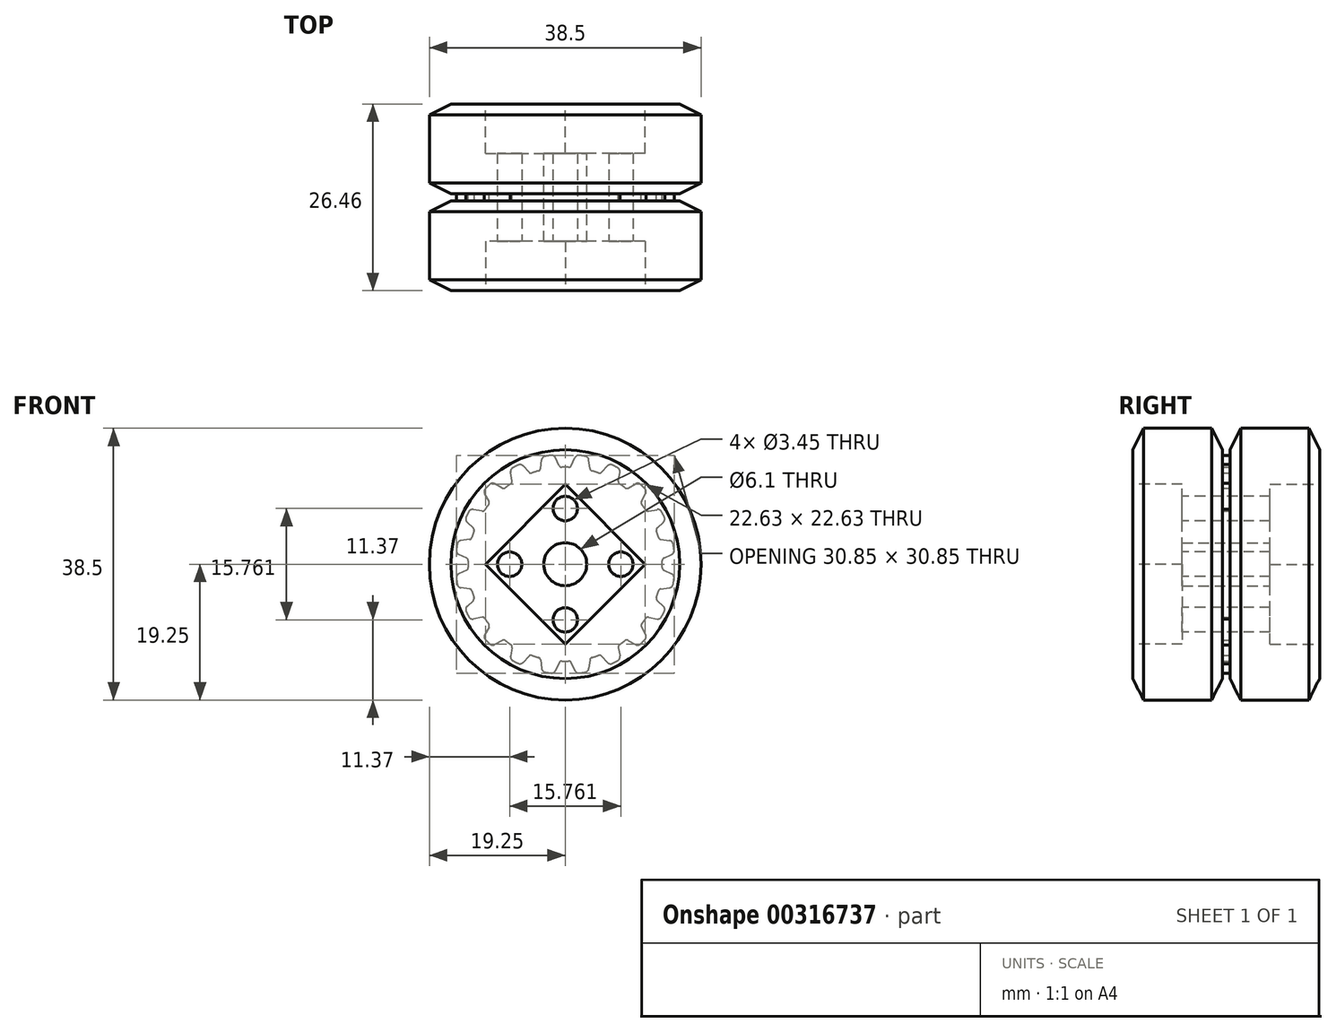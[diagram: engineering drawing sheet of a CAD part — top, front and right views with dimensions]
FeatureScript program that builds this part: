
annotation { "Feature Type Name" : "Feature", "Feature Type Description" : "" }
export const myFeature = defineFeature(function(context is Context, id is Id, definition is map)
    precondition{}
    {
        {
            var Q0;
            Q0=qCreatedBy(makeId("Front.planeOp"),FACE);
            var sketch = newSketch(context, id + "F0", { "sketchPlane" : qUnion([Q0])});
            skArc(sketch, "E0", {"start": v(-2, 15.42) * mm, "mid": v(-2.43, 15.36) * mm, "end": v(-2.86, 15.29) * mm});
            skArc(sketch, "E1", {"start": v(0.49, 13.74) * mm, "mid": v(0, 13.75) * mm, "end": v(-0.49, 13.74) * mm});
            skLineSegment(sketch, "E2", {"start": v(0, 0) * mm, "end": v(0, 13.75) * mm, "construction": true});
            skLineSegment(sketch, "E3", {"start": v(0.86, 13.97) * mm, "end": v(1.38, 15.08) * mm});
            skLineSegment(sketch, "E4", {"start": v(-0.86, 13.97) * mm, "end": v(-1.38, 15.08) * mm});
            skLineSegment(sketch, "E5", {"start": v(0, 13.75) * mm, "end": v(0, 15.55) * mm, "construction": true});
            skPoint(sketch, "E6.visualSharp", {"position": v(-1.56, 15.47) * mm});
            skArc(sketch, "E6.filletArc", {"start": v(-1.38, 15.08) * mm, "mid": v(-1.63, 15.35) * mm, "end": v(-2, 15.42) * mm});
            skPoint(sketch, "E7.visualSharp", {"position": v(1.56, 15.47) * mm});
            skArc(sketch, "E7.filletArc", {"start": v(2, 15.42) * mm, "mid": v(1.63, 15.35) * mm, "end": v(1.38, 15.08) * mm});
            skPoint(sketch, "E8.visualSharp", {"position": v(-0.75, 13.73) * mm});
            skArc(sketch, "E8.filletArc", {"start": v(-0.86, 13.97) * mm, "mid": v(-0.7, 13.8) * mm, "end": v(-0.49, 13.74) * mm});
            skPoint(sketch, "E9.visualSharp", {"position": v(0.75, 13.73) * mm});
            skArc(sketch, "E9.filletArc", {"start": v(0.49, 13.74) * mm, "mid": v(0.7, 13.8) * mm, "end": v(0.86, 13.97) * mm});
            skLineSegment(sketch, "E10.1.0", {"start": v(-4.25, 13.08) * mm, "end": v(-4.8, 14.8) * mm, "construction": true});
            skLineSegment(sketch, "E10.1.1", {"start": v(-5.14, 13.02) * mm, "end": v(-5.97, 13.92) * mm});
            skPoint(sketch, "E10.1.2", {"position": v(-6.27, 14.23) * mm});
            skPoint(sketch, "E10.1.3", {"position": v(-3.53, 13.3) * mm});
            skPoint(sketch, "E10.1.4", {"position": v(-4.96, 12.83) * mm});
            skPoint(sketch, "E10.1.5", {"position": v(-3.3, 15.2) * mm});
            skLineSegment(sketch, "E10.1.6", {"start": v(-3.5, 13.56) * mm, "end": v(-3.35, 14.77) * mm});
            skArc(sketch, "E10.1.7", {"start": v(-5.97, 13.92) * mm, "mid": v(-6.3, 14.1) * mm, "end": v(-6.67, 14.05) * mm});
            skArc(sketch, "E10.1.8", {"start": v(-2.86, 15.29) * mm, "mid": v(-3.2, 15.1) * mm, "end": v(-3.35, 14.77) * mm});
            skArc(sketch, "E10.1.9", {"start": v(-3.78, 13.22) * mm, "mid": v(-4.25, 13.08) * mm, "end": v(-4.7, 12.92) * mm});
            skArc(sketch, "E10.1.10", {"start": v(-3.78, 13.22) * mm, "mid": v(-3.6, 13.35) * mm, "end": v(-3.5, 13.56) * mm});
            skArc(sketch, "E10.1.11", {"start": v(-5.14, 13.02) * mm, "mid": v(-4.94, 12.9) * mm, "end": v(-4.7, 12.92) * mm});
            skLineSegment(sketch, "E10.2.0", {"start": v(-8.08, 11.13) * mm, "end": v(-9.14, 12.58) * mm, "construction": true});
            skLineSegment(sketch, "E10.2.1", {"start": v(-8.91, 10.8) * mm, "end": v(-9.98, 11.4) * mm});
            skPoint(sketch, "E10.2.2", {"position": v(-10.36, 11.6) * mm});
            skPoint(sketch, "E10.2.3", {"position": v(-7.46, 11.55) * mm});
            skPoint(sketch, "E10.2.4", {"position": v(-8.68, 10.67) * mm});
            skPoint(sketch, "E10.2.5", {"position": v(-7.83, 13.44) * mm});
            skLineSegment(sketch, "E10.2.6", {"start": v(-7.52, 11.81) * mm, "end": v(-7.75, 13.01) * mm});
            skArc(sketch, "E10.2.7", {"start": v(-9.98, 11.4) * mm, "mid": v(-10.35, 11.46) * mm, "end": v(-10.68, 11.3) * mm});
            skArc(sketch, "E10.2.8", {"start": v(-7.45, 13.65) * mm, "mid": v(-7.7, 13.38) * mm, "end": v(-7.75, 13.01) * mm});
            skArc(sketch, "E10.2.9", {"start": v(-7.68, 11.4) * mm, "mid": v(-8.08, 11.13) * mm, "end": v(-8.47, 10.83) * mm});
            skArc(sketch, "E10.2.10", {"start": v(-7.68, 11.4) * mm, "mid": v(-7.54, 11.58) * mm, "end": v(-7.52, 11.81) * mm});
            skArc(sketch, "E10.2.11", {"start": v(-8.91, 10.8) * mm, "mid": v(-8.69, 10.75) * mm, "end": v(-8.47, 10.83) * mm});
            skLineSegment(sketch, "E10.3.0", {"start": v(-11.13, 8.08) * mm, "end": v(-12.58, 9.14) * mm, "construction": true});
            skLineSegment(sketch, "E10.3.1", {"start": v(-11.81, 7.52) * mm, "end": v(-13.01, 7.75) * mm});
            skPoint(sketch, "E10.3.2", {"position": v(-13.44, 7.83) * mm});
            skPoint(sketch, "E10.3.3", {"position": v(-10.67, 8.68) * mm});
            skPoint(sketch, "E10.3.4", {"position": v(-11.55, 7.46) * mm});
            skPoint(sketch, "E10.3.5", {"position": v(-11.6, 10.36) * mm});
            skLineSegment(sketch, "E10.3.6", {"start": v(-10.8, 8.91) * mm, "end": v(-11.4, 9.98) * mm});
            skArc(sketch, "E10.3.7", {"start": v(-13.01, 7.75) * mm, "mid": v(-13.38, 7.7) * mm, "end": v(-13.65, 7.45) * mm});
            skArc(sketch, "E10.3.8", {"start": v(-11.3, 10.68) * mm, "mid": v(-11.46, 10.35) * mm, "end": v(-11.4, 9.98) * mm});
            skArc(sketch, "E10.3.9", {"start": v(-10.83, 8.47) * mm, "mid": v(-11.13, 8.08) * mm, "end": v(-11.4, 7.68) * mm});
            skArc(sketch, "E10.3.10", {"start": v(-10.83, 8.47) * mm, "mid": v(-10.75, 8.69) * mm, "end": v(-10.8, 8.91) * mm});
            skArc(sketch, "E10.3.11", {"start": v(-11.81, 7.52) * mm, "mid": v(-11.58, 7.54) * mm, "end": v(-11.4, 7.68) * mm});
            skLineSegment(sketch, "E10.4.0", {"start": v(-13.08, 4.25) * mm, "end": v(-14.8, 4.8) * mm, "construction": true});
            skLineSegment(sketch, "E10.4.1", {"start": v(-13.56, 3.5) * mm, "end": v(-14.77, 3.35) * mm});
            skPoint(sketch, "E10.4.2", {"position": v(-15.2, 3.3) * mm});
            skPoint(sketch, "E10.4.3", {"position": v(-12.83, 4.96) * mm});
            skPoint(sketch, "E10.4.4", {"position": v(-13.3, 3.53) * mm});
            skPoint(sketch, "E10.4.5", {"position": v(-14.23, 6.27) * mm});
            skLineSegment(sketch, "E10.4.6", {"start": v(-13.02, 5.14) * mm, "end": v(-13.92, 5.97) * mm});
            skArc(sketch, "E10.4.7", {"start": v(-14.77, 3.35) * mm, "mid": v(-15.1, 3.2) * mm, "end": v(-15.29, 2.86) * mm});
            skArc(sketch, "E10.4.8", {"start": v(-14.05, 6.67) * mm, "mid": v(-14.1, 6.3) * mm, "end": v(-13.92, 5.97) * mm});
            skArc(sketch, "E10.4.9", {"start": v(-12.92, 4.7) * mm, "mid": v(-13.08, 4.25) * mm, "end": v(-13.22, 3.78) * mm});
            skArc(sketch, "E10.4.10", {"start": v(-12.92, 4.7) * mm, "mid": v(-12.9, 4.94) * mm, "end": v(-13.02, 5.14) * mm});
            skArc(sketch, "E10.4.11", {"start": v(-13.56, 3.5) * mm, "mid": v(-13.35, 3.6) * mm, "end": v(-13.22, 3.78) * mm});
            skLineSegment(sketch, "E10.5.0", {"start": v(-13.75, 0) * mm, "end": v(-15.55, 0) * mm, "construction": true});
            skLineSegment(sketch, "E10.5.1", {"start": v(-13.97, -0.86) * mm, "end": v(-15.08, -1.38) * mm});
            skPoint(sketch, "E10.5.2", {"position": v(-15.47, -1.56) * mm});
            skPoint(sketch, "E10.5.3", {"position": v(-13.73, 0.75) * mm});
            skPoint(sketch, "E10.5.4", {"position": v(-13.73, -0.75) * mm});
            skPoint(sketch, "E10.5.5", {"position": v(-15.47, 1.56) * mm});
            skLineSegment(sketch, "E10.5.6", {"start": v(-13.97, 0.86) * mm, "end": v(-15.08, 1.38) * mm});
            skArc(sketch, "E10.5.7", {"start": v(-15.08, -1.38) * mm, "mid": v(-15.35, -1.63) * mm, "end": v(-15.42, -2) * mm});
            skArc(sketch, "E10.5.8", {"start": v(-15.42, 2) * mm, "mid": v(-15.35, 1.63) * mm, "end": v(-15.08, 1.38) * mm});
            skArc(sketch, "E10.5.9", {"start": v(-13.74, 0.49) * mm, "mid": v(-13.75, 0) * mm, "end": v(-13.74, -0.49) * mm});
            skArc(sketch, "E10.5.10", {"start": v(-13.74, 0.49) * mm, "mid": v(-13.8, 0.7) * mm, "end": v(-13.97, 0.86) * mm});
            skArc(sketch, "E10.5.11", {"start": v(-13.97, -0.86) * mm, "mid": v(-13.8, -0.7) * mm, "end": v(-13.74, -0.49) * mm});
            skLineSegment(sketch, "E10.6.0", {"start": v(-13.08, -4.25) * mm, "end": v(-14.8, -4.8) * mm, "construction": true});
            skLineSegment(sketch, "E10.6.1", {"start": v(-13.02, -5.14) * mm, "end": v(-13.92, -5.97) * mm});
            skPoint(sketch, "E10.6.2", {"position": v(-14.23, -6.27) * mm});
            skPoint(sketch, "E10.6.3", {"position": v(-13.3, -3.53) * mm});
            skPoint(sketch, "E10.6.4", {"position": v(-12.83, -4.96) * mm});
            skPoint(sketch, "E10.6.5", {"position": v(-15.2, -3.3) * mm});
            skLineSegment(sketch, "E10.6.6", {"start": v(-13.56, -3.5) * mm, "end": v(-14.77, -3.35) * mm});
            skArc(sketch, "E10.6.7", {"start": v(-13.92, -5.97) * mm, "mid": v(-14.1, -6.3) * mm, "end": v(-14.05, -6.67) * mm});
            skArc(sketch, "E10.6.8", {"start": v(-15.29, -2.86) * mm, "mid": v(-15.1, -3.2) * mm, "end": v(-14.77, -3.35) * mm});
            skArc(sketch, "E10.6.9", {"start": v(-13.22, -3.78) * mm, "mid": v(-13.08, -4.25) * mm, "end": v(-12.92, -4.7) * mm});
            skArc(sketch, "E10.6.10", {"start": v(-13.22, -3.78) * mm, "mid": v(-13.35, -3.6) * mm, "end": v(-13.56, -3.5) * mm});
            skArc(sketch, "E10.6.11", {"start": v(-13.02, -5.14) * mm, "mid": v(-12.9, -4.94) * mm, "end": v(-12.92, -4.7) * mm});
            skLineSegment(sketch, "E10.7.0", {"start": v(-11.13, -8.08) * mm, "end": v(-12.58, -9.14) * mm, "construction": true});
            skLineSegment(sketch, "E10.7.1", {"start": v(-10.8, -8.91) * mm, "end": v(-11.4, -9.98) * mm});
            skPoint(sketch, "E10.7.2", {"position": v(-11.6, -10.36) * mm});
            skPoint(sketch, "E10.7.3", {"position": v(-11.55, -7.46) * mm});
            skPoint(sketch, "E10.7.4", {"position": v(-10.67, -8.68) * mm});
            skPoint(sketch, "E10.7.5", {"position": v(-13.44, -7.83) * mm});
            skLineSegment(sketch, "E10.7.6", {"start": v(-11.81, -7.52) * mm, "end": v(-13.01, -7.75) * mm});
            skArc(sketch, "E10.7.7", {"start": v(-11.4, -9.98) * mm, "mid": v(-11.46, -10.35) * mm, "end": v(-11.3, -10.68) * mm});
            skArc(sketch, "E10.7.8", {"start": v(-13.65, -7.45) * mm, "mid": v(-13.38, -7.7) * mm, "end": v(-13.01, -7.75) * mm});
            skArc(sketch, "E10.7.9", {"start": v(-11.4, -7.68) * mm, "mid": v(-11.13, -8.08) * mm, "end": v(-10.83, -8.47) * mm});
            skArc(sketch, "E10.7.10", {"start": v(-11.4, -7.68) * mm, "mid": v(-11.58, -7.54) * mm, "end": v(-11.81, -7.52) * mm});
            skArc(sketch, "E10.7.11", {"start": v(-10.8, -8.91) * mm, "mid": v(-10.75, -8.69) * mm, "end": v(-10.83, -8.47) * mm});
            skLineSegment(sketch, "E10.8.0", {"start": v(-8.08, -11.13) * mm, "end": v(-9.14, -12.58) * mm, "construction": true});
            skLineSegment(sketch, "E10.8.1", {"start": v(-7.52, -11.81) * mm, "end": v(-7.75, -13.01) * mm});
            skPoint(sketch, "E10.8.2", {"position": v(-7.83, -13.44) * mm});
            skPoint(sketch, "E10.8.3", {"position": v(-8.68, -10.67) * mm});
            skPoint(sketch, "E10.8.4", {"position": v(-7.46, -11.55) * mm});
            skPoint(sketch, "E10.8.5", {"position": v(-10.36, -11.6) * mm});
            skLineSegment(sketch, "E10.8.6", {"start": v(-8.91, -10.8) * mm, "end": v(-9.98, -11.4) * mm});
            skArc(sketch, "E10.8.7", {"start": v(-7.75, -13.01) * mm, "mid": v(-7.7, -13.38) * mm, "end": v(-7.45, -13.65) * mm});
            skArc(sketch, "E10.8.8", {"start": v(-10.68, -11.3) * mm, "mid": v(-10.35, -11.46) * mm, "end": v(-9.98, -11.4) * mm});
            skArc(sketch, "E10.8.9", {"start": v(-8.47, -10.83) * mm, "mid": v(-8.08, -11.13) * mm, "end": v(-7.68, -11.4) * mm});
            skArc(sketch, "E10.8.10", {"start": v(-8.47, -10.83) * mm, "mid": v(-8.69, -10.75) * mm, "end": v(-8.91, -10.8) * mm});
            skArc(sketch, "E10.8.11", {"start": v(-7.52, -11.81) * mm, "mid": v(-7.54, -11.58) * mm, "end": v(-7.68, -11.4) * mm});
            skLineSegment(sketch, "E10.9.0", {"start": v(-4.25, -13.08) * mm, "end": v(-4.8, -14.8) * mm, "construction": true});
            skLineSegment(sketch, "E10.9.1", {"start": v(-3.5, -13.56) * mm, "end": v(-3.35, -14.77) * mm});
            skPoint(sketch, "E10.9.2", {"position": v(-3.3, -15.2) * mm});
            skPoint(sketch, "E10.9.3", {"position": v(-4.96, -12.83) * mm});
            skPoint(sketch, "E10.9.4", {"position": v(-3.53, -13.3) * mm});
            skPoint(sketch, "E10.9.5", {"position": v(-6.27, -14.23) * mm});
            skLineSegment(sketch, "E10.9.6", {"start": v(-5.14, -13.02) * mm, "end": v(-5.97, -13.92) * mm});
            skArc(sketch, "E10.9.7", {"start": v(-3.35, -14.77) * mm, "mid": v(-3.2, -15.1) * mm, "end": v(-2.86, -15.29) * mm});
            skArc(sketch, "E10.9.8", {"start": v(-6.67, -14.05) * mm, "mid": v(-6.3, -14.1) * mm, "end": v(-5.97, -13.92) * mm});
            skArc(sketch, "E10.9.9", {"start": v(-4.7, -12.92) * mm, "mid": v(-4.25, -13.08) * mm, "end": v(-3.78, -13.22) * mm});
            skArc(sketch, "E10.9.10", {"start": v(-4.7, -12.92) * mm, "mid": v(-4.94, -12.9) * mm, "end": v(-5.14, -13.02) * mm});
            skArc(sketch, "E10.9.11", {"start": v(-3.5, -13.56) * mm, "mid": v(-3.6, -13.35) * mm, "end": v(-3.78, -13.22) * mm});
            skLineSegment(sketch, "E10.10.0", {"start": v(0, -13.75) * mm, "end": v(0, -15.55) * mm, "construction": true});
            skLineSegment(sketch, "E10.10.1", {"start": v(0.86, -13.97) * mm, "end": v(1.38, -15.08) * mm});
            skPoint(sketch, "E10.10.2", {"position": v(1.56, -15.47) * mm});
            skPoint(sketch, "E10.10.3", {"position": v(-0.75, -13.73) * mm});
            skPoint(sketch, "E10.10.4", {"position": v(0.75, -13.73) * mm});
            skPoint(sketch, "E10.10.5", {"position": v(-1.56, -15.47) * mm});
            skLineSegment(sketch, "E10.10.6", {"start": v(-0.86, -13.97) * mm, "end": v(-1.38, -15.08) * mm});
            skArc(sketch, "E10.10.7", {"start": v(1.38, -15.08) * mm, "mid": v(1.63, -15.35) * mm, "end": v(2, -15.42) * mm});
            skArc(sketch, "E10.10.8", {"start": v(-2, -15.42) * mm, "mid": v(-1.63, -15.35) * mm, "end": v(-1.38, -15.08) * mm});
            skArc(sketch, "E10.10.9", {"start": v(-0.49, -13.74) * mm, "mid": v(0, -13.75) * mm, "end": v(0.49, -13.74) * mm});
            skArc(sketch, "E10.10.10", {"start": v(-0.49, -13.74) * mm, "mid": v(-0.7, -13.8) * mm, "end": v(-0.86, -13.97) * mm});
            skArc(sketch, "E10.10.11", {"start": v(0.86, -13.97) * mm, "mid": v(0.7, -13.8) * mm, "end": v(0.49, -13.74) * mm});
            skLineSegment(sketch, "E10.11.0", {"start": v(4.25, -13.08) * mm, "end": v(4.8, -14.8) * mm, "construction": true});
            skLineSegment(sketch, "E10.11.1", {"start": v(5.14, -13.02) * mm, "end": v(5.97, -13.92) * mm});
            skPoint(sketch, "E10.11.2", {"position": v(6.27, -14.23) * mm});
            skPoint(sketch, "E10.11.3", {"position": v(3.53, -13.3) * mm});
            skPoint(sketch, "E10.11.4", {"position": v(4.96, -12.83) * mm});
            skPoint(sketch, "E10.11.5", {"position": v(3.3, -15.2) * mm});
            skLineSegment(sketch, "E10.11.6", {"start": v(3.5, -13.56) * mm, "end": v(3.35, -14.77) * mm});
            skArc(sketch, "E10.11.7", {"start": v(5.97, -13.92) * mm, "mid": v(6.3, -14.1) * mm, "end": v(6.67, -14.05) * mm});
            skArc(sketch, "E10.11.8", {"start": v(2.86, -15.29) * mm, "mid": v(3.2, -15.1) * mm, "end": v(3.35, -14.77) * mm});
            skArc(sketch, "E10.11.9", {"start": v(3.78, -13.22) * mm, "mid": v(4.25, -13.08) * mm, "end": v(4.7, -12.92) * mm});
            skArc(sketch, "E10.11.10", {"start": v(3.78, -13.22) * mm, "mid": v(3.6, -13.35) * mm, "end": v(3.5, -13.56) * mm});
            skArc(sketch, "E10.11.11", {"start": v(5.14, -13.02) * mm, "mid": v(4.94, -12.9) * mm, "end": v(4.7, -12.92) * mm});
            skLineSegment(sketch, "E10.12.0", {"start": v(8.08, -11.13) * mm, "end": v(9.14, -12.58) * mm, "construction": true});
            skLineSegment(sketch, "E10.12.1", {"start": v(8.91, -10.8) * mm, "end": v(9.98, -11.4) * mm});
            skPoint(sketch, "E10.12.2", {"position": v(10.36, -11.6) * mm});
            skPoint(sketch, "E10.12.3", {"position": v(7.46, -11.55) * mm});
            skPoint(sketch, "E10.12.4", {"position": v(8.68, -10.67) * mm});
            skPoint(sketch, "E10.12.5", {"position": v(7.83, -13.44) * mm});
            skLineSegment(sketch, "E10.12.6", {"start": v(7.52, -11.81) * mm, "end": v(7.75, -13.01) * mm});
            skArc(sketch, "E10.12.7", {"start": v(9.98, -11.4) * mm, "mid": v(10.35, -11.46) * mm, "end": v(10.68, -11.3) * mm});
            skArc(sketch, "E10.12.8", {"start": v(7.45, -13.65) * mm, "mid": v(7.7, -13.38) * mm, "end": v(7.75, -13.01) * mm});
            skArc(sketch, "E10.12.9", {"start": v(7.68, -11.4) * mm, "mid": v(8.08, -11.13) * mm, "end": v(8.47, -10.83) * mm});
            skArc(sketch, "E10.12.10", {"start": v(7.68, -11.4) * mm, "mid": v(7.54, -11.58) * mm, "end": v(7.52, -11.81) * mm});
            skArc(sketch, "E10.12.11", {"start": v(8.91, -10.8) * mm, "mid": v(8.69, -10.75) * mm, "end": v(8.47, -10.83) * mm});
            skLineSegment(sketch, "E10.13.0", {"start": v(11.13, -8.08) * mm, "end": v(12.58, -9.14) * mm, "construction": true});
            skLineSegment(sketch, "E10.13.1", {"start": v(11.81, -7.52) * mm, "end": v(13.01, -7.75) * mm});
            skPoint(sketch, "E10.13.2", {"position": v(13.44, -7.83) * mm});
            skPoint(sketch, "E10.13.3", {"position": v(10.67, -8.68) * mm});
            skPoint(sketch, "E10.13.4", {"position": v(11.55, -7.46) * mm});
            skPoint(sketch, "E10.13.5", {"position": v(11.6, -10.36) * mm});
            skLineSegment(sketch, "E10.13.6", {"start": v(10.8, -8.91) * mm, "end": v(11.4, -9.98) * mm});
            skArc(sketch, "E10.13.7", {"start": v(13.01, -7.75) * mm, "mid": v(13.38, -7.7) * mm, "end": v(13.65, -7.45) * mm});
            skArc(sketch, "E10.13.8", {"start": v(11.3, -10.68) * mm, "mid": v(11.46, -10.35) * mm, "end": v(11.4, -9.98) * mm});
            skArc(sketch, "E10.13.9", {"start": v(10.83, -8.47) * mm, "mid": v(11.13, -8.08) * mm, "end": v(11.4, -7.68) * mm});
            skArc(sketch, "E10.13.10", {"start": v(10.83, -8.47) * mm, "mid": v(10.75, -8.69) * mm, "end": v(10.8, -8.91) * mm});
            skArc(sketch, "E10.13.11", {"start": v(11.81, -7.52) * mm, "mid": v(11.58, -7.54) * mm, "end": v(11.4, -7.68) * mm});
            skLineSegment(sketch, "E10.14.0", {"start": v(13.08, -4.25) * mm, "end": v(14.8, -4.8) * mm, "construction": true});
            skLineSegment(sketch, "E10.14.1", {"start": v(13.56, -3.5) * mm, "end": v(14.77, -3.35) * mm});
            skPoint(sketch, "E10.14.2", {"position": v(15.2, -3.3) * mm});
            skPoint(sketch, "E10.14.3", {"position": v(12.83, -4.96) * mm});
            skPoint(sketch, "E10.14.4", {"position": v(13.3, -3.53) * mm});
            skPoint(sketch, "E10.14.5", {"position": v(14.23, -6.27) * mm});
            skLineSegment(sketch, "E10.14.6", {"start": v(13.02, -5.14) * mm, "end": v(13.92, -5.97) * mm});
            skArc(sketch, "E10.14.7", {"start": v(14.77, -3.35) * mm, "mid": v(15.1, -3.2) * mm, "end": v(15.29, -2.86) * mm});
            skArc(sketch, "E10.14.8", {"start": v(14.05, -6.67) * mm, "mid": v(14.1, -6.3) * mm, "end": v(13.92, -5.97) * mm});
            skArc(sketch, "E10.14.9", {"start": v(12.92, -4.7) * mm, "mid": v(13.08, -4.25) * mm, "end": v(13.22, -3.78) * mm});
            skArc(sketch, "E10.14.10", {"start": v(12.92, -4.7) * mm, "mid": v(12.9, -4.94) * mm, "end": v(13.02, -5.14) * mm});
            skArc(sketch, "E10.14.11", {"start": v(13.56, -3.5) * mm, "mid": v(13.35, -3.6) * mm, "end": v(13.22, -3.78) * mm});
            skLineSegment(sketch, "E10.15.0", {"start": v(13.75, 0) * mm, "end": v(15.55, 0) * mm, "construction": true});
            skLineSegment(sketch, "E10.15.1", {"start": v(13.97, 0.86) * mm, "end": v(15.08, 1.38) * mm});
            skPoint(sketch, "E10.15.2", {"position": v(15.47, 1.56) * mm});
            skPoint(sketch, "E10.15.3", {"position": v(13.73, -0.75) * mm});
            skPoint(sketch, "E10.15.4", {"position": v(13.73, 0.75) * mm});
            skPoint(sketch, "E10.15.5", {"position": v(15.47, -1.56) * mm});
            skLineSegment(sketch, "E10.15.6", {"start": v(13.97, -0.86) * mm, "end": v(15.08, -1.38) * mm});
            skArc(sketch, "E10.15.7", {"start": v(15.08, 1.38) * mm, "mid": v(15.35, 1.63) * mm, "end": v(15.42, 2) * mm});
            skArc(sketch, "E10.15.8", {"start": v(15.42, -2) * mm, "mid": v(15.35, -1.63) * mm, "end": v(15.08, -1.38) * mm});
            skArc(sketch, "E10.15.9", {"start": v(13.74, -0.49) * mm, "mid": v(13.75, 0) * mm, "end": v(13.74, 0.49) * mm});
            skArc(sketch, "E10.15.10", {"start": v(13.74, -0.49) * mm, "mid": v(13.8, -0.7) * mm, "end": v(13.97, -0.86) * mm});
            skArc(sketch, "E10.15.11", {"start": v(13.97, 0.86) * mm, "mid": v(13.8, 0.7) * mm, "end": v(13.74, 0.49) * mm});
            skArc(sketch, "E11.trimOffspring", {"start": v(2.86, 15.29) * mm, "mid": v(2.43, 15.36) * mm, "end": v(2, 15.42) * mm});
            skArc(sketch, "E12.trimOffspring", {"start": v(15.29, -2.86) * mm, "mid": v(15.36, -2.43) * mm, "end": v(15.42, -2) * mm});
            skArc(sketch, "E13.trimOffspring", {"start": v(13.65, -7.45) * mm, "mid": v(13.86, -7.06) * mm, "end": v(14.05, -6.67) * mm});
            skArc(sketch, "E14.trimOffspring", {"start": v(10.68, -11.3) * mm, "mid": v(11, -11) * mm, "end": v(11.3, -10.68) * mm});
            skArc(sketch, "E15.trimOffspring", {"start": v(6.67, -14.05) * mm, "mid": v(7.06, -13.86) * mm, "end": v(7.45, -13.65) * mm});
            skArc(sketch, "E16.trimOffspring", {"start": v(2, -15.42) * mm, "mid": v(2.43, -15.36) * mm, "end": v(2.86, -15.29) * mm});
            skArc(sketch, "E17.trimOffspring", {"start": v(-2.86, -15.29) * mm, "mid": v(-2.43, -15.36) * mm, "end": v(-2, -15.42) * mm});
            skArc(sketch, "E18.trimOffspring", {"start": v(-7.45, -13.65) * mm, "mid": v(-7.06, -13.86) * mm, "end": v(-6.67, -14.05) * mm});
            skArc(sketch, "E19.trimOffspring", {"start": v(-11.3, -10.68) * mm, "mid": v(-11, -11) * mm, "end": v(-10.68, -11.3) * mm});
            skArc(sketch, "E20.trimOffspring", {"start": v(-14.05, -6.67) * mm, "mid": v(-13.86, -7.06) * mm, "end": v(-13.65, -7.45) * mm});
            skArc(sketch, "E21.trimOffspring", {"start": v(-15.42, -2) * mm, "mid": v(-15.36, -2.43) * mm, "end": v(-15.29, -2.86) * mm});
            skArc(sketch, "E22.trimOffspring", {"start": v(-15.29, 2.86) * mm, "mid": v(-15.36, 2.43) * mm, "end": v(-15.42, 2) * mm});
            skArc(sketch, "E23.trimOffspring", {"start": v(-13.65, 7.45) * mm, "mid": v(-13.86, 7.06) * mm, "end": v(-14.05, 6.67) * mm});
            skArc(sketch, "E24.trimOffspring", {"start": v(-10.68, 11.3) * mm, "mid": v(-11, 11) * mm, "end": v(-11.3, 10.68) * mm});
            skArc(sketch, "E25.trimOffspring", {"start": v(-6.67, 14.05) * mm, "mid": v(-7.06, 13.86) * mm, "end": v(-7.45, 13.65) * mm});
            skArc(sketch, "E26", {"start": v(14.05, 6.67) * mm, "mid": v(13.86, 7.06) * mm, "end": v(13.65, 7.45) * mm, "construction": true});
            skCircle(sketch, "E27", {"center": v(0, 0) * mm, "radius": 13.75 * mm, "construction": true});
            skCircle(sketch, "E28", {"center": v(0, 0) * mm, "radius": 15.98 * mm, "construction": true});
            skLineSegment(sketch, "E29", {"start": v(0, 15.55) * mm, "end": v(0, 15.98) * mm, "construction": true});
            skLineSegment(sketch, "E30", {"start": v(4.8, 14.8) * mm, "end": v(4.94, 15.2) * mm, "construction": true});
            skLineSegment(sketch, "E31.3.16.0", {"start": v(13.02, 5.14) * mm, "end": v(13.92, 5.97) * mm});
            skPoint(sketch, "E31.6.16.0", {"position": v(14.23, 6.27) * mm});
            skPoint(sketch, "E31.7.16.0", {"position": v(13.3, 3.53) * mm});
            skPoint(sketch, "E31.8.16.0", {"position": v(12.83, 4.96) * mm});
            skPoint(sketch, "E31.9.16.0", {"position": v(15.2, 3.3) * mm});
            skLineSegment(sketch, "E31.10.16.0", {"start": v(13.56, 3.5) * mm, "end": v(14.77, 3.35) * mm});
            skArc(sketch, "E31.13.16.0", {"start": v(13.92, 5.97) * mm, "mid": v(14.1, 6.3) * mm, "end": v(14.05, 6.67) * mm});
            skLineSegment(sketch, "E31.14.16.0", {"start": v(13.08, 4.25) * mm, "end": v(14.8, 4.8) * mm, "construction": true});
            skArc(sketch, "E31.17.16.0", {"start": v(15.29, 2.86) * mm, "mid": v(15.1, 3.2) * mm, "end": v(14.77, 3.35) * mm});
            skArc(sketch, "E31.21.16.0", {"start": v(13.22, 3.78) * mm, "mid": v(13.08, 4.25) * mm, "end": v(12.92, 4.7) * mm});
            skArc(sketch, "E31.25.16.0", {"start": v(13.22, 3.78) * mm, "mid": v(13.35, 3.6) * mm, "end": v(13.56, 3.5) * mm});
            skArc(sketch, "E31.29.16.0", {"start": v(13.02, 5.14) * mm, "mid": v(12.9, 4.94) * mm, "end": v(12.92, 4.7) * mm});
            skLineSegment(sketch, "E31.3.17.0", {"start": v(10.8, 8.91) * mm, "end": v(11.4, 9.98) * mm});
            skPoint(sketch, "E31.6.17.0", {"position": v(11.6, 10.36) * mm});
            skPoint(sketch, "E31.7.17.0", {"position": v(11.55, 7.46) * mm});
            skPoint(sketch, "E31.8.17.0", {"position": v(10.67, 8.68) * mm});
            skPoint(sketch, "E31.9.17.0", {"position": v(13.44, 7.83) * mm});
            skLineSegment(sketch, "E31.10.17.0", {"start": v(11.81, 7.52) * mm, "end": v(13.01, 7.75) * mm});
            skArc(sketch, "E31.13.17.0", {"start": v(11.4, 9.98) * mm, "mid": v(11.46, 10.35) * mm, "end": v(11.3, 10.68) * mm});
            skLineSegment(sketch, "E31.14.17.0", {"start": v(11.13, 8.08) * mm, "end": v(12.58, 9.14) * mm, "construction": true});
            skArc(sketch, "E31.17.17.0", {"start": v(13.65, 7.45) * mm, "mid": v(13.38, 7.7) * mm, "end": v(13.01, 7.75) * mm});
            skArc(sketch, "E31.21.17.0", {"start": v(11.4, 7.68) * mm, "mid": v(11.13, 8.08) * mm, "end": v(10.83, 8.47) * mm});
            skArc(sketch, "E31.25.17.0", {"start": v(11.4, 7.68) * mm, "mid": v(11.58, 7.54) * mm, "end": v(11.81, 7.52) * mm});
            skArc(sketch, "E31.29.17.0", {"start": v(10.8, 8.91) * mm, "mid": v(10.75, 8.69) * mm, "end": v(10.83, 8.47) * mm});
            skLineSegment(sketch, "E31.3.18.0", {"start": v(7.52, 11.81) * mm, "end": v(7.75, 13.01) * mm});
            skPoint(sketch, "E31.7.18.0", {"position": v(8.68, 10.67) * mm});
            skPoint(sketch, "E31.8.18.0", {"position": v(7.46, 11.55) * mm});
            skPoint(sketch, "E31.9.18.0", {"position": v(10.36, 11.6) * mm});
            skLineSegment(sketch, "E31.10.18.0", {"start": v(8.91, 10.8) * mm, "end": v(9.98, 11.4) * mm});
            skArc(sketch, "E31.13.18.0", {"start": v(7.75, 13.01) * mm, "mid": v(7.7, 13.38) * mm, "end": v(7.45, 13.65) * mm});
            skLineSegment(sketch, "E31.14.18.0", {"start": v(8.08, 11.13) * mm, "end": v(9.14, 12.58) * mm, "construction": true});
            skArc(sketch, "E31.17.18.0", {"start": v(10.68, 11.3) * mm, "mid": v(10.35, 11.46) * mm, "end": v(9.98, 11.4) * mm});
            skArc(sketch, "E31.21.18.0", {"start": v(8.47, 10.83) * mm, "mid": v(8.08, 11.13) * mm, "end": v(7.68, 11.4) * mm});
            skArc(sketch, "E31.25.18.0", {"start": v(8.47, 10.83) * mm, "mid": v(8.69, 10.75) * mm, "end": v(8.91, 10.8) * mm});
            skArc(sketch, "E31.29.18.0", {"start": v(7.52, 11.81) * mm, "mid": v(7.54, 11.58) * mm, "end": v(7.68, 11.4) * mm});
            skLineSegment(sketch, "E31.3.19.0", {"start": v(3.5, 13.56) * mm, "end": v(3.35, 14.77) * mm});
            skPoint(sketch, "E31.6.19.0", {"position": v(3.3, 15.2) * mm});
            skPoint(sketch, "E31.7.19.0", {"position": v(4.96, 12.83) * mm});
            skPoint(sketch, "E31.8.19.0", {"position": v(3.53, 13.3) * mm});
            skPoint(sketch, "E31.9.19.0", {"position": v(6.27, 14.23) * mm});
            skLineSegment(sketch, "E31.10.19.0", {"start": v(5.14, 13.02) * mm, "end": v(5.97, 13.92) * mm});
            skArc(sketch, "E31.13.19.0", {"start": v(3.35, 14.77) * mm, "mid": v(3.2, 15.1) * mm, "end": v(2.86, 15.29) * mm});
            skLineSegment(sketch, "E31.14.19.0", {"start": v(4.25, 13.08) * mm, "end": v(4.8, 14.8) * mm, "construction": true});
            skArc(sketch, "E31.17.19.0", {"start": v(6.67, 14.05) * mm, "mid": v(6.3, 14.1) * mm, "end": v(5.97, 13.92) * mm});
            skArc(sketch, "E31.21.19.0", {"start": v(4.7, 12.92) * mm, "mid": v(4.25, 13.08) * mm, "end": v(3.78, 13.22) * mm});
            skArc(sketch, "E31.25.19.0", {"start": v(4.7, 12.92) * mm, "mid": v(4.94, 12.9) * mm, "end": v(5.14, 13.02) * mm});
            skArc(sketch, "E31.29.19.0", {"start": v(3.5, 13.56) * mm, "mid": v(3.6, 13.35) * mm, "end": v(3.78, 13.22) * mm});
            skArc(sketch, "E32.trimOffspring", {"start": v(14.05, 6.67) * mm, "mid": v(13.86, 7.06) * mm, "end": v(13.65, 7.45) * mm});
            skArc(sketch, "E33.trimOffspring", {"start": v(7.45, 13.65) * mm, "mid": v(-13.86, -7.06) * mm, "end": v(15.42, -2) * mm, "construction": true});
            skArc(sketch, "E34.trimOffspring", {"start": v(7.45, 13.65) * mm, "mid": v(7.06, 13.86) * mm, "end": v(6.67, 14.05) * mm});
            skArc(sketch, "E35.trimOffspring", {"start": v(11.3, 10.68) * mm, "mid": v(11, 11) * mm, "end": v(10.68, 11.3) * mm, "construction": true});
            skArc(sketch, "E36.trimOffspring", {"start": v(11.3, 10.68) * mm, "mid": v(11, 11) * mm, "end": v(10.68, 11.3) * mm});
            skArc(sketch, "E37.trimOffspring", {"start": v(15.42, 2) * mm, "mid": v(15.36, 2.43) * mm, "end": v(15.29, 2.86) * mm, "construction": true});
            skArc(sketch, "E38.trimOffspring", {"start": v(15.42, 2) * mm, "mid": v(15.36, 2.43) * mm, "end": v(15.29, 2.86) * mm});
            skSolve(sketch);
        }
        {
            var Q0;
            Q0 = qSketchRegion(id + "F0", true);
            extrude(context, id + "F1", {"entities" : qUnion([Q0]), "depth" : ((27 / 25.4) / 2) * mm});
        }
        {
            var Q0;
            Q0=makeQuery(id+"F1.opExtrude","CAP_FACE",FACE,{"disambiguationData":[OSD([sQuery(id+"F0.wireOp",EDGE,"E0"),sQuery(id+"F0.wireOp",EDGE,"E1"),sQuery(id+"F0.wireOp",EDGE,"E3"),sQuery(id+"F0.wireOp",EDGE,"E4"),sQuery(id+"F0.wireOp",EDGE,"E6.filletArc"),sQuery(id+"F0.wireOp",EDGE,"E7.filletArc"),sQuery(id+"F0.wireOp",EDGE,"E8.filletArc"),sQuery(id+"F0.wireOp",EDGE,"E9.filletArc"),sQuery(id+"F0.wireOp",EDGE,"E10.1.1"),sQuery(id+"F0.wireOp",EDGE,"E10.1.6"),sQuery(id+"F0.wireOp",EDGE,"E10.1.7"),sQuery(id+"F0.wireOp",EDGE,"E10.1.8"),sQuery(id+"F0.wireOp",EDGE,"E10.1.9"),sQuery(id+"F0.wireOp",EDGE,"E10.1.10"),sQuery(id+"F0.wireOp",EDGE,"E10.1.11"),sQuery(id+"F0.wireOp",EDGE,"E10.2.1"),sQuery(id+"F0.wireOp",EDGE,"E10.2.6"),sQuery(id+"F0.wireOp",EDGE,"E10.2.7"),sQuery(id+"F0.wireOp",EDGE,"E10.2.8"),sQuery(id+"F0.wireOp",EDGE,"E10.2.9"),sQuery(id+"F0.wireOp",EDGE,"E10.2.10"),sQuery(id+"F0.wireOp",EDGE,"E10.2.11"),sQuery(id+"F0.wireOp",EDGE,"E10.3.1"),sQuery(id+"F0.wireOp",EDGE,"E10.3.6"),sQuery(id+"F0.wireOp",EDGE,"E10.3.7"),sQuery(id+"F0.wireOp",EDGE,"E10.3.8"),sQuery(id+"F0.wireOp",EDGE,"E10.3.9"),sQuery(id+"F0.wireOp",EDGE,"E10.3.10"),sQuery(id+"F0.wireOp",EDGE,"E10.3.11"),sQuery(id+"F0.wireOp",EDGE,"E10.4.1"),sQuery(id+"F0.wireOp",EDGE,"E10.4.6"),sQuery(id+"F0.wireOp",EDGE,"E10.4.7"),sQuery(id+"F0.wireOp",EDGE,"E10.4.8"),sQuery(id+"F0.wireOp",EDGE,"E10.4.9"),sQuery(id+"F0.wireOp",EDGE,"E10.4.10"),sQuery(id+"F0.wireOp",EDGE,"E10.4.11"),sQuery(id+"F0.wireOp",EDGE,"E10.5.1"),sQuery(id+"F0.wireOp",EDGE,"E10.5.6"),sQuery(id+"F0.wireOp",EDGE,"E10.5.7"),sQuery(id+"F0.wireOp",EDGE,"E10.5.8"),sQuery(id+"F0.wireOp",EDGE,"E10.5.9"),sQuery(id+"F0.wireOp",EDGE,"E10.5.10"),sQuery(id+"F0.wireOp",EDGE,"E10.5.11"),sQuery(id+"F0.wireOp",EDGE,"E10.6.1"),sQuery(id+"F0.wireOp",EDGE,"E10.6.6"),sQuery(id+"F0.wireOp",EDGE,"E10.6.7"),sQuery(id+"F0.wireOp",EDGE,"E10.6.8"),sQuery(id+"F0.wireOp",EDGE,"E10.6.9"),sQuery(id+"F0.wireOp",EDGE,"E10.6.10"),sQuery(id+"F0.wireOp",EDGE,"E10.6.11"),sQuery(id+"F0.wireOp",EDGE,"E10.7.1"),sQuery(id+"F0.wireOp",EDGE,"E10.7.6"),sQuery(id+"F0.wireOp",EDGE,"E10.7.7"),sQuery(id+"F0.wireOp",EDGE,"E10.7.8"),sQuery(id+"F0.wireOp",EDGE,"E10.7.9"),sQuery(id+"F0.wireOp",EDGE,"E10.7.10"),sQuery(id+"F0.wireOp",EDGE,"E10.7.11"),sQuery(id+"F0.wireOp",EDGE,"E10.8.1"),sQuery(id+"F0.wireOp",EDGE,"E10.8.6"),sQuery(id+"F0.wireOp",EDGE,"E10.8.7"),sQuery(id+"F0.wireOp",EDGE,"E10.8.8"),sQuery(id+"F0.wireOp",EDGE,"E10.8.9"),sQuery(id+"F0.wireOp",EDGE,"E10.8.10"),sQuery(id+"F0.wireOp",EDGE,"E10.8.11"),sQuery(id+"F0.wireOp",EDGE,"E10.9.1"),sQuery(id+"F0.wireOp",EDGE,"E10.9.6"),sQuery(id+"F0.wireOp",EDGE,"E10.9.7"),sQuery(id+"F0.wireOp",EDGE,"E10.9.8"),sQuery(id+"F0.wireOp",EDGE,"E10.9.9"),sQuery(id+"F0.wireOp",EDGE,"E10.9.10"),sQuery(id+"F0.wireOp",EDGE,"E10.9.11"),sQuery(id+"F0.wireOp",EDGE,"E10.10.1"),sQuery(id+"F0.wireOp",EDGE,"E10.10.6"),sQuery(id+"F0.wireOp",EDGE,"E10.10.7"),sQuery(id+"F0.wireOp",EDGE,"E10.10.8"),sQuery(id+"F0.wireOp",EDGE,"E10.10.9"),sQuery(id+"F0.wireOp",EDGE,"E10.10.10"),sQuery(id+"F0.wireOp",EDGE,"E10.10.11"),sQuery(id+"F0.wireOp",EDGE,"E10.11.1"),sQuery(id+"F0.wireOp",EDGE,"E10.11.6"),sQuery(id+"F0.wireOp",EDGE,"E10.11.7"),sQuery(id+"F0.wireOp",EDGE,"E10.11.8"),sQuery(id+"F0.wireOp",EDGE,"E10.11.9"),sQuery(id+"F0.wireOp",EDGE,"E10.11.10"),sQuery(id+"F0.wireOp",EDGE,"E10.11.11"),sQuery(id+"F0.wireOp",EDGE,"E10.12.1"),sQuery(id+"F0.wireOp",EDGE,"E10.12.6"),sQuery(id+"F0.wireOp",EDGE,"E10.12.7"),sQuery(id+"F0.wireOp",EDGE,"E10.12.8"),sQuery(id+"F0.wireOp",EDGE,"E10.12.9"),sQuery(id+"F0.wireOp",EDGE,"E10.12.10"),sQuery(id+"F0.wireOp",EDGE,"E10.12.11"),sQuery(id+"F0.wireOp",EDGE,"E10.13.1"),sQuery(id+"F0.wireOp",EDGE,"E10.13.6"),sQuery(id+"F0.wireOp",EDGE,"E10.13.7"),sQuery(id+"F0.wireOp",EDGE,"E10.13.8"),sQuery(id+"F0.wireOp",EDGE,"E10.13.9"),sQuery(id+"F0.wireOp",EDGE,"E10.13.10"),sQuery(id+"F0.wireOp",EDGE,"E10.13.11"),sQuery(id+"F0.wireOp",EDGE,"E10.14.1"),sQuery(id+"F0.wireOp",EDGE,"E10.14.6"),sQuery(id+"F0.wireOp",EDGE,"E10.14.7"),sQuery(id+"F0.wireOp",EDGE,"E10.14.8"),sQuery(id+"F0.wireOp",EDGE,"E10.14.9"),sQuery(id+"F0.wireOp",EDGE,"E10.14.10"),sQuery(id+"F0.wireOp",EDGE,"E10.14.11"),sQuery(id+"F0.wireOp",EDGE,"E10.15.1"),sQuery(id+"F0.wireOp",EDGE,"E10.15.6"),sQuery(id+"F0.wireOp",EDGE,"E10.15.7"),sQuery(id+"F0.wireOp",EDGE,"E10.15.8"),sQuery(id+"F0.wireOp",EDGE,"E10.15.9"),sQuery(id+"F0.wireOp",EDGE,"E10.15.10"),sQuery(id+"F0.wireOp",EDGE,"E10.15.11"),sQuery(id+"F0.wireOp",EDGE,"E11.trimOffspring"),sQuery(id+"F0.wireOp",EDGE,"E12.trimOffspring"),sQuery(id+"F0.wireOp",EDGE,"E13.trimOffspring"),sQuery(id+"F0.wireOp",EDGE,"E14.trimOffspring"),sQuery(id+"F0.wireOp",EDGE,"E15.trimOffspring"),sQuery(id+"F0.wireOp",EDGE,"E16.trimOffspring"),sQuery(id+"F0.wireOp",EDGE,"E17.trimOffspring"),sQuery(id+"F0.wireOp",EDGE,"E18.trimOffspring"),sQuery(id+"F0.wireOp",EDGE,"E19.trimOffspring"),sQuery(id+"F0.wireOp",EDGE,"E20.trimOffspring"),sQuery(id+"F0.wireOp",EDGE,"E21.trimOffspring"),sQuery(id+"F0.wireOp",EDGE,"E22.trimOffspring"),sQuery(id+"F0.wireOp",EDGE,"E23.trimOffspring"),sQuery(id+"F0.wireOp",EDGE,"E24.trimOffspring"),sQuery(id+"F0.wireOp",EDGE,"E25.trimOffspring")])],"isStart":false});
            var sketch = newSketch(context, id + "F2", { "sketchPlane" : qUnion([Q0])});
            skCircle(sketch, "E39", {"center": v(0, 0) * mm, "radius": 19.25 * mm});
            skLineSegment(sketch, "E40", {"start": v(0, 0) * mm, "end": v(2.43, 15.36) * mm, "construction": true});
            skLineSegment(sketch, "E41", {"start": v(2.43, 15.36) * mm, "end": v(3.01, 19.02) * mm, "construction": true});
            skSolve(sketch);
        }
        {
            var Q0;
            Q0 = qSketchRegion(id + "F2", true);
            extrude(context, id + "F3", {"entities" : qUnion([Q0]), "operationType" : NewBodyOperationType.ADD, "depth" : 12.7 * mm});
        }
        {
            var Q0;
            Q0=makeQuery(id+"F3.opExtrude","CAP_EDGE",EDGE,{"disambiguationData":[OSD([sQuery(id+"F2.wireOp",EDGE,"E39")])],"isStart":true});
            var Q1;
            Q1=makeQuery(id+"F3.opExtrude","CAP_EDGE",EDGE,{"disambiguationData":[OSD([sQuery(id+"F2.wireOp",EDGE,"E39")])],"isStart":false});
            chamfer(context, id + "F4", {"entities" : qUnion([Q0, Q1]), "chamferType" : ChamferType.TWO_OFFSETS, "width1" : 1.52 * mm, "oppositeDirection" : false, "width2" : 3.05 * mm, "tangentPropagation" : true});
        }
        {
            var Q0;
            Q0=makeQuery(id+"F1.opExtrude","CAP_FACE",FACE,{"disambiguationData":[OSD([sQuery(id+"F0.wireOp",EDGE,"E0"),sQuery(id+"F0.wireOp",EDGE,"E1"),sQuery(id+"F0.wireOp",EDGE,"E3"),sQuery(id+"F0.wireOp",EDGE,"E4"),sQuery(id+"F0.wireOp",EDGE,"E6.filletArc"),sQuery(id+"F0.wireOp",EDGE,"E7.filletArc"),sQuery(id+"F0.wireOp",EDGE,"E8.filletArc"),sQuery(id+"F0.wireOp",EDGE,"E9.filletArc"),sQuery(id+"F0.wireOp",EDGE,"E10.1.1"),sQuery(id+"F0.wireOp",EDGE,"E10.1.6"),sQuery(id+"F0.wireOp",EDGE,"E10.1.7"),sQuery(id+"F0.wireOp",EDGE,"E10.1.8"),sQuery(id+"F0.wireOp",EDGE,"E10.1.9"),sQuery(id+"F0.wireOp",EDGE,"E10.1.10"),sQuery(id+"F0.wireOp",EDGE,"E10.1.11"),sQuery(id+"F0.wireOp",EDGE,"E10.2.1"),sQuery(id+"F0.wireOp",EDGE,"E10.2.6"),sQuery(id+"F0.wireOp",EDGE,"E10.2.7"),sQuery(id+"F0.wireOp",EDGE,"E10.2.8"),sQuery(id+"F0.wireOp",EDGE,"E10.2.9"),sQuery(id+"F0.wireOp",EDGE,"E10.2.10"),sQuery(id+"F0.wireOp",EDGE,"E10.2.11"),sQuery(id+"F0.wireOp",EDGE,"E10.3.1"),sQuery(id+"F0.wireOp",EDGE,"E10.3.6"),sQuery(id+"F0.wireOp",EDGE,"E10.3.7"),sQuery(id+"F0.wireOp",EDGE,"E10.3.8"),sQuery(id+"F0.wireOp",EDGE,"E10.3.9"),sQuery(id+"F0.wireOp",EDGE,"E10.3.10"),sQuery(id+"F0.wireOp",EDGE,"E10.3.11"),sQuery(id+"F0.wireOp",EDGE,"E10.4.1"),sQuery(id+"F0.wireOp",EDGE,"E10.4.6"),sQuery(id+"F0.wireOp",EDGE,"E10.4.7"),sQuery(id+"F0.wireOp",EDGE,"E10.4.8"),sQuery(id+"F0.wireOp",EDGE,"E10.4.9"),sQuery(id+"F0.wireOp",EDGE,"E10.4.10"),sQuery(id+"F0.wireOp",EDGE,"E10.4.11"),sQuery(id+"F0.wireOp",EDGE,"E10.5.1"),sQuery(id+"F0.wireOp",EDGE,"E10.5.6"),sQuery(id+"F0.wireOp",EDGE,"E10.5.7"),sQuery(id+"F0.wireOp",EDGE,"E10.5.8"),sQuery(id+"F0.wireOp",EDGE,"E10.5.9"),sQuery(id+"F0.wireOp",EDGE,"E10.5.10"),sQuery(id+"F0.wireOp",EDGE,"E10.5.11"),sQuery(id+"F0.wireOp",EDGE,"E10.6.1"),sQuery(id+"F0.wireOp",EDGE,"E10.6.6"),sQuery(id+"F0.wireOp",EDGE,"E10.6.7"),sQuery(id+"F0.wireOp",EDGE,"E10.6.8"),sQuery(id+"F0.wireOp",EDGE,"E10.6.9"),sQuery(id+"F0.wireOp",EDGE,"E10.6.10"),sQuery(id+"F0.wireOp",EDGE,"E10.6.11"),sQuery(id+"F0.wireOp",EDGE,"E10.7.1"),sQuery(id+"F0.wireOp",EDGE,"E10.7.6"),sQuery(id+"F0.wireOp",EDGE,"E10.7.7"),sQuery(id+"F0.wireOp",EDGE,"E10.7.8"),sQuery(id+"F0.wireOp",EDGE,"E10.7.9"),sQuery(id+"F0.wireOp",EDGE,"E10.7.10"),sQuery(id+"F0.wireOp",EDGE,"E10.7.11"),sQuery(id+"F0.wireOp",EDGE,"E10.8.1"),sQuery(id+"F0.wireOp",EDGE,"E10.8.6"),sQuery(id+"F0.wireOp",EDGE,"E10.8.7"),sQuery(id+"F0.wireOp",EDGE,"E10.8.8"),sQuery(id+"F0.wireOp",EDGE,"E10.8.9"),sQuery(id+"F0.wireOp",EDGE,"E10.8.10"),sQuery(id+"F0.wireOp",EDGE,"E10.8.11"),sQuery(id+"F0.wireOp",EDGE,"E10.9.1"),sQuery(id+"F0.wireOp",EDGE,"E10.9.6"),sQuery(id+"F0.wireOp",EDGE,"E10.9.7"),sQuery(id+"F0.wireOp",EDGE,"E10.9.8"),sQuery(id+"F0.wireOp",EDGE,"E10.9.9"),sQuery(id+"F0.wireOp",EDGE,"E10.9.10"),sQuery(id+"F0.wireOp",EDGE,"E10.9.11"),sQuery(id+"F0.wireOp",EDGE,"E10.10.1"),sQuery(id+"F0.wireOp",EDGE,"E10.10.6"),sQuery(id+"F0.wireOp",EDGE,"E10.10.7"),sQuery(id+"F0.wireOp",EDGE,"E10.10.8"),sQuery(id+"F0.wireOp",EDGE,"E10.10.9"),sQuery(id+"F0.wireOp",EDGE,"E10.10.10"),sQuery(id+"F0.wireOp",EDGE,"E10.10.11"),sQuery(id+"F0.wireOp",EDGE,"E10.11.1"),sQuery(id+"F0.wireOp",EDGE,"E10.11.6"),sQuery(id+"F0.wireOp",EDGE,"E10.11.7"),sQuery(id+"F0.wireOp",EDGE,"E10.11.8"),sQuery(id+"F0.wireOp",EDGE,"E10.11.9"),sQuery(id+"F0.wireOp",EDGE,"E10.11.10"),sQuery(id+"F0.wireOp",EDGE,"E10.11.11"),sQuery(id+"F0.wireOp",EDGE,"E10.12.1"),sQuery(id+"F0.wireOp",EDGE,"E10.12.6"),sQuery(id+"F0.wireOp",EDGE,"E10.12.7"),sQuery(id+"F0.wireOp",EDGE,"E10.12.8"),sQuery(id+"F0.wireOp",EDGE,"E10.12.9"),sQuery(id+"F0.wireOp",EDGE,"E10.12.10"),sQuery(id+"F0.wireOp",EDGE,"E10.12.11"),sQuery(id+"F0.wireOp",EDGE,"E10.13.1"),sQuery(id+"F0.wireOp",EDGE,"E10.13.6"),sQuery(id+"F0.wireOp",EDGE,"E10.13.7"),sQuery(id+"F0.wireOp",EDGE,"E10.13.8"),sQuery(id+"F0.wireOp",EDGE,"E10.13.9"),sQuery(id+"F0.wireOp",EDGE,"E10.13.10"),sQuery(id+"F0.wireOp",EDGE,"E10.13.11"),sQuery(id+"F0.wireOp",EDGE,"E10.14.1"),sQuery(id+"F0.wireOp",EDGE,"E10.14.6"),sQuery(id+"F0.wireOp",EDGE,"E10.14.7"),sQuery(id+"F0.wireOp",EDGE,"E10.14.8"),sQuery(id+"F0.wireOp",EDGE,"E10.14.9"),sQuery(id+"F0.wireOp",EDGE,"E10.14.10"),sQuery(id+"F0.wireOp",EDGE,"E10.14.11"),sQuery(id+"F0.wireOp",EDGE,"E10.15.1"),sQuery(id+"F0.wireOp",EDGE,"E10.15.6"),sQuery(id+"F0.wireOp",EDGE,"E10.15.7"),sQuery(id+"F0.wireOp",EDGE,"E10.15.8"),sQuery(id+"F0.wireOp",EDGE,"E10.15.9"),sQuery(id+"F0.wireOp",EDGE,"E10.15.10"),sQuery(id+"F0.wireOp",EDGE,"E10.15.11"),sQuery(id+"F0.wireOp",EDGE,"E11.trimOffspring"),sQuery(id+"F0.wireOp",EDGE,"E12.trimOffspring"),sQuery(id+"F0.wireOp",EDGE,"E13.trimOffspring"),sQuery(id+"F0.wireOp",EDGE,"E14.trimOffspring"),sQuery(id+"F0.wireOp",EDGE,"E15.trimOffspring"),sQuery(id+"F0.wireOp",EDGE,"E16.trimOffspring"),sQuery(id+"F0.wireOp",EDGE,"E17.trimOffspring"),sQuery(id+"F0.wireOp",EDGE,"E18.trimOffspring"),sQuery(id+"F0.wireOp",EDGE,"E19.trimOffspring"),sQuery(id+"F0.wireOp",EDGE,"E20.trimOffspring"),sQuery(id+"F0.wireOp",EDGE,"E21.trimOffspring"),sQuery(id+"F0.wireOp",EDGE,"E22.trimOffspring"),sQuery(id+"F0.wireOp",EDGE,"E23.trimOffspring"),sQuery(id+"F0.wireOp",EDGE,"E24.trimOffspring"),sQuery(id+"F0.wireOp",EDGE,"E25.trimOffspring")])],"isStart":true});
            var sketch = newSketch(context, id + "F5", { "sketchPlane" : qUnion([Q0])});
            skCircle(sketch, "E42", {"center": v(0, 0) * mm, "radius": 3.05 * mm});
            skSolve(sketch);
        }
        {
            var Q0;
            Q0 = qSketchRegion(id + "F5", true);
            extrude(context, id + "F6", {"entities" : qUnion([Q0]), "operationType" : NewBodyOperationType.REMOVE, "endBound" : BoundingType.THROUGH_ALL, "oppositeDirection" : true, "depth" : 25.4 * mm});
        }
        {
            var Q0;
            Q0=makeQuery(id+"F3.opExtrude","CAP_FACE",FACE,{"disambiguationData":[OSD([sQuery(id+"F2.wireOp",EDGE,"E39")])],"isStart":false});
            var sketch = newSketch(context, id + "F7", { "sketchPlane" : qUnion([Q0])});
            skCircle(sketch, "E43", {"center": v(0, 7.88) * mm, "radius": 1.73 * mm});
            skCircle(sketch, "E44", {"center": v(-7.88, 0) * mm, "radius": 1.73 * mm});
            skCircle(sketch, "E45", {"center": v(0, -7.88) * mm, "radius": 1.73 * mm});
            skCircle(sketch, "E46", {"center": v(7.88, 0) * mm, "radius": 1.73 * mm});
            skCircle(sketch, "E47", {"center": v(0, 0) * mm, "radius": 7.88 * mm, "construction": true});
            skSolve(sketch);
        }
        {
            var Q0;
            Q0 = qSketchRegion(id + "F7", true);
            extrude(context, id + "F8", {"entities" : qUnion([Q0]), "operationType" : NewBodyOperationType.REMOVE, "endBound" : BoundingType.THROUGH_ALL, "oppositeDirection" : true, "depth" : 25.4 * mm});
        }
        {
            var Q0;
            Q0=makeQuery(id+"F3.opExtrude","CAP_FACE",FACE,{"disambiguationData":[OSD([sQuery(id+"F2.wireOp",EDGE,"E39")])],"isStart":false});
            var sketch = newSketch(context, id + "F9", { "sketchPlane" : qUnion([Q0])});
            skLineSegment(sketch, "E48", {"start": v(0, 11.32) * mm, "end": v(-11.32, 0) * mm});
            skLineSegment(sketch, "E49", {"start": v(-11.32, 0) * mm, "end": v(0, -11.32) * mm});
            skLineSegment(sketch, "E50", {"start": v(0, -11.32) * mm, "end": v(11.32, 0) * mm});
            skLineSegment(sketch, "E51", {"start": v(11.32, 0) * mm, "end": v(0, 11.32) * mm});
            skSolve(sketch);
        }
        {
            var Q0;
            Q0 = qSketchRegion(id + "F9", true);
            extrude(context, id + "F10", {"entities" : qUnion([Q0]), "operationType" : NewBodyOperationType.REMOVE, "oppositeDirection" : true, "depth" : 7 * mm});
        }
        {
            var Q0;
            Q0=makeQuery(id+"F10.boolean.opBoolean","COPY",FACE,{"derivedFrom":makeQuery(id+"F10.opExtrude","SWEPT_FACE",FACE,{"disambiguationData":[OSD([sQuery(id+"F9.wireOp",EDGE,"E49")])]})});
            var sketch = newSketch(context, id + "F11", { "sketchPlane" : qUnion([Q0])});
            skArc(sketch, "E52", {"start": v(-22.7, -2.54) * mm, "mid": v(-20.16, 0) * mm, "end": v(-22.7, 2.54) * mm});
            skLineSegment(sketch, "E53", {"start": v(-22.7, 2.54) * mm, "end": v(-26.2, 2.54) * mm});
            skLineSegment(sketch, "E54", {"start": v(-26.2, 2.54) * mm, "end": v(-26.2, -2.54) * mm});
            skLineSegment(sketch, "E55", {"start": v(-26.2, -2.54) * mm, "end": v(-22.7, -2.54) * mm});
            skSolve(sketch);
        }
        {
            var Q0;
            Q0=makeQuery(id+"F11.imprint","IMPRINT",FACE,{"disambiguationData":[TD([[makeQuery(id+"F11.imprint","IMPRINT",EDGE,{"derivedFrom":sQuery(id+"F11.wireOp",EDGE,"E52")}),1.0]])]});
            extrude(context, id + "F12", {"entities" : qUnion([Q0]), "operationType" : NewBodyOperationType.REMOVE, "endBound" : BoundingType.THROUGH_ALL, "oppositeDirection" : true, "depth" : 25.4 * mm});
        }
        {
            var Q0;
            Q0=makeQuery(id+"F1.opExtrude","SWEPT_BODY",BODY,{"disambiguationData":[OSD([sQuery(id+"F0.wireOp",EDGE,"E0"),sQuery(id+"F0.wireOp",EDGE,"E1"),sQuery(id+"F0.wireOp",EDGE,"E3"),sQuery(id+"F0.wireOp",EDGE,"E4"),sQuery(id+"F0.wireOp",EDGE,"E6.filletArc"),sQuery(id+"F0.wireOp",EDGE,"E7.filletArc"),sQuery(id+"F0.wireOp",EDGE,"E8.filletArc"),sQuery(id+"F0.wireOp",EDGE,"E9.filletArc"),sQuery(id+"F0.wireOp",EDGE,"E10.1.1"),sQuery(id+"F0.wireOp",EDGE,"E10.1.6"),sQuery(id+"F0.wireOp",EDGE,"E10.1.7"),sQuery(id+"F0.wireOp",EDGE,"E10.1.8"),sQuery(id+"F0.wireOp",EDGE,"E10.1.9"),sQuery(id+"F0.wireOp",EDGE,"E10.1.10"),sQuery(id+"F0.wireOp",EDGE,"E10.1.11"),sQuery(id+"F0.wireOp",EDGE,"E10.2.1"),sQuery(id+"F0.wireOp",EDGE,"E10.2.6"),sQuery(id+"F0.wireOp",EDGE,"E10.2.7"),sQuery(id+"F0.wireOp",EDGE,"E10.2.8"),sQuery(id+"F0.wireOp",EDGE,"E10.2.9"),sQuery(id+"F0.wireOp",EDGE,"E10.2.10"),sQuery(id+"F0.wireOp",EDGE,"E10.2.11"),sQuery(id+"F0.wireOp",EDGE,"E10.3.1"),sQuery(id+"F0.wireOp",EDGE,"E10.3.6"),sQuery(id+"F0.wireOp",EDGE,"E10.3.7"),sQuery(id+"F0.wireOp",EDGE,"E10.3.8"),sQuery(id+"F0.wireOp",EDGE,"E10.3.9"),sQuery(id+"F0.wireOp",EDGE,"E10.3.10"),sQuery(id+"F0.wireOp",EDGE,"E10.3.11"),sQuery(id+"F0.wireOp",EDGE,"E10.4.1"),sQuery(id+"F0.wireOp",EDGE,"E10.4.6"),sQuery(id+"F0.wireOp",EDGE,"E10.4.7"),sQuery(id+"F0.wireOp",EDGE,"E10.4.8"),sQuery(id+"F0.wireOp",EDGE,"E10.4.9"),sQuery(id+"F0.wireOp",EDGE,"E10.4.10"),sQuery(id+"F0.wireOp",EDGE,"E10.4.11"),sQuery(id+"F0.wireOp",EDGE,"E10.5.1"),sQuery(id+"F0.wireOp",EDGE,"E10.5.6"),sQuery(id+"F0.wireOp",EDGE,"E10.5.7"),sQuery(id+"F0.wireOp",EDGE,"E10.5.8"),sQuery(id+"F0.wireOp",EDGE,"E10.5.9"),sQuery(id+"F0.wireOp",EDGE,"E10.5.10"),sQuery(id+"F0.wireOp",EDGE,"E10.5.11"),sQuery(id+"F0.wireOp",EDGE,"E10.6.1"),sQuery(id+"F0.wireOp",EDGE,"E10.6.6"),sQuery(id+"F0.wireOp",EDGE,"E10.6.7"),sQuery(id+"F0.wireOp",EDGE,"E10.6.8"),sQuery(id+"F0.wireOp",EDGE,"E10.6.9"),sQuery(id+"F0.wireOp",EDGE,"E10.6.10"),sQuery(id+"F0.wireOp",EDGE,"E10.6.11"),sQuery(id+"F0.wireOp",EDGE,"E10.7.1"),sQuery(id+"F0.wireOp",EDGE,"E10.7.6"),sQuery(id+"F0.wireOp",EDGE,"E10.7.7"),sQuery(id+"F0.wireOp",EDGE,"E10.7.8"),sQuery(id+"F0.wireOp",EDGE,"E10.7.9"),sQuery(id+"F0.wireOp",EDGE,"E10.7.10"),sQuery(id+"F0.wireOp",EDGE,"E10.7.11"),sQuery(id+"F0.wireOp",EDGE,"E10.8.1"),sQuery(id+"F0.wireOp",EDGE,"E10.8.6"),sQuery(id+"F0.wireOp",EDGE,"E10.8.7"),sQuery(id+"F0.wireOp",EDGE,"E10.8.8"),sQuery(id+"F0.wireOp",EDGE,"E10.8.9"),sQuery(id+"F0.wireOp",EDGE,"E10.8.10"),sQuery(id+"F0.wireOp",EDGE,"E10.8.11"),sQuery(id+"F0.wireOp",EDGE,"E10.9.1"),sQuery(id+"F0.wireOp",EDGE,"E10.9.6"),sQuery(id+"F0.wireOp",EDGE,"E10.9.7"),sQuery(id+"F0.wireOp",EDGE,"E10.9.8"),sQuery(id+"F0.wireOp",EDGE,"E10.9.9"),sQuery(id+"F0.wireOp",EDGE,"E10.9.10"),sQuery(id+"F0.wireOp",EDGE,"E10.9.11"),sQuery(id+"F0.wireOp",EDGE,"E10.10.1"),sQuery(id+"F0.wireOp",EDGE,"E10.10.6"),sQuery(id+"F0.wireOp",EDGE,"E10.10.7"),sQuery(id+"F0.wireOp",EDGE,"E10.10.8"),sQuery(id+"F0.wireOp",EDGE,"E10.10.9"),sQuery(id+"F0.wireOp",EDGE,"E10.10.10"),sQuery(id+"F0.wireOp",EDGE,"E10.10.11"),sQuery(id+"F0.wireOp",EDGE,"E10.11.1"),sQuery(id+"F0.wireOp",EDGE,"E10.11.6"),sQuery(id+"F0.wireOp",EDGE,"E10.11.7"),sQuery(id+"F0.wireOp",EDGE,"E10.11.8"),sQuery(id+"F0.wireOp",EDGE,"E10.11.9"),sQuery(id+"F0.wireOp",EDGE,"E10.11.10"),sQuery(id+"F0.wireOp",EDGE,"E10.11.11"),sQuery(id+"F0.wireOp",EDGE,"E10.12.1"),sQuery(id+"F0.wireOp",EDGE,"E10.12.6"),sQuery(id+"F0.wireOp",EDGE,"E10.12.7"),sQuery(id+"F0.wireOp",EDGE,"E10.12.8"),sQuery(id+"F0.wireOp",EDGE,"E10.12.9"),sQuery(id+"F0.wireOp",EDGE,"E10.12.10"),sQuery(id+"F0.wireOp",EDGE,"E10.12.11"),sQuery(id+"F0.wireOp",EDGE,"E10.13.1"),sQuery(id+"F0.wireOp",EDGE,"E10.13.6"),sQuery(id+"F0.wireOp",EDGE,"E10.13.7"),sQuery(id+"F0.wireOp",EDGE,"E10.13.8"),sQuery(id+"F0.wireOp",EDGE,"E10.13.9"),sQuery(id+"F0.wireOp",EDGE,"E10.13.10"),sQuery(id+"F0.wireOp",EDGE,"E10.13.11"),sQuery(id+"F0.wireOp",EDGE,"E10.14.1"),sQuery(id+"F0.wireOp",EDGE,"E10.14.6"),sQuery(id+"F0.wireOp",EDGE,"E10.14.7"),sQuery(id+"F0.wireOp",EDGE,"E10.14.8"),sQuery(id+"F0.wireOp",EDGE,"E10.14.9"),sQuery(id+"F0.wireOp",EDGE,"E10.14.10"),sQuery(id+"F0.wireOp",EDGE,"E10.14.11"),sQuery(id+"F0.wireOp",EDGE,"E10.15.1"),sQuery(id+"F0.wireOp",EDGE,"E10.15.6"),sQuery(id+"F0.wireOp",EDGE,"E10.15.7"),sQuery(id+"F0.wireOp",EDGE,"E10.15.8"),sQuery(id+"F0.wireOp",EDGE,"E10.15.9"),sQuery(id+"F0.wireOp",EDGE,"E10.15.10"),sQuery(id+"F0.wireOp",EDGE,"E10.15.11"),sQuery(id+"F0.wireOp",EDGE,"E11.trimOffspring"),sQuery(id+"F0.wireOp",EDGE,"E12.trimOffspring"),sQuery(id+"F0.wireOp",EDGE,"E13.trimOffspring"),sQuery(id+"F0.wireOp",EDGE,"E14.trimOffspring"),sQuery(id+"F0.wireOp",EDGE,"E15.trimOffspring"),sQuery(id+"F0.wireOp",EDGE,"E16.trimOffspring"),sQuery(id+"F0.wireOp",EDGE,"E17.trimOffspring"),sQuery(id+"F0.wireOp",EDGE,"E18.trimOffspring"),sQuery(id+"F0.wireOp",EDGE,"E19.trimOffspring"),sQuery(id+"F0.wireOp",EDGE,"E20.trimOffspring"),sQuery(id+"F0.wireOp",EDGE,"E21.trimOffspring"),sQuery(id+"F0.wireOp",EDGE,"E22.trimOffspring"),sQuery(id+"F0.wireOp",EDGE,"E23.trimOffspring"),sQuery(id+"F0.wireOp",EDGE,"E24.trimOffspring"),sQuery(id+"F0.wireOp",EDGE,"E25.trimOffspring")])]});
            var Q1;
            Q1=qCreatedBy(makeId("Front.planeOp"),FACE);
            mirror(context, id + "F13", {"operationType" : NewBodyOperationType.ADD, "entities" : qUnion([Q0]), "mirrorPlane" : qUnion([Q1])});
        }
    });
